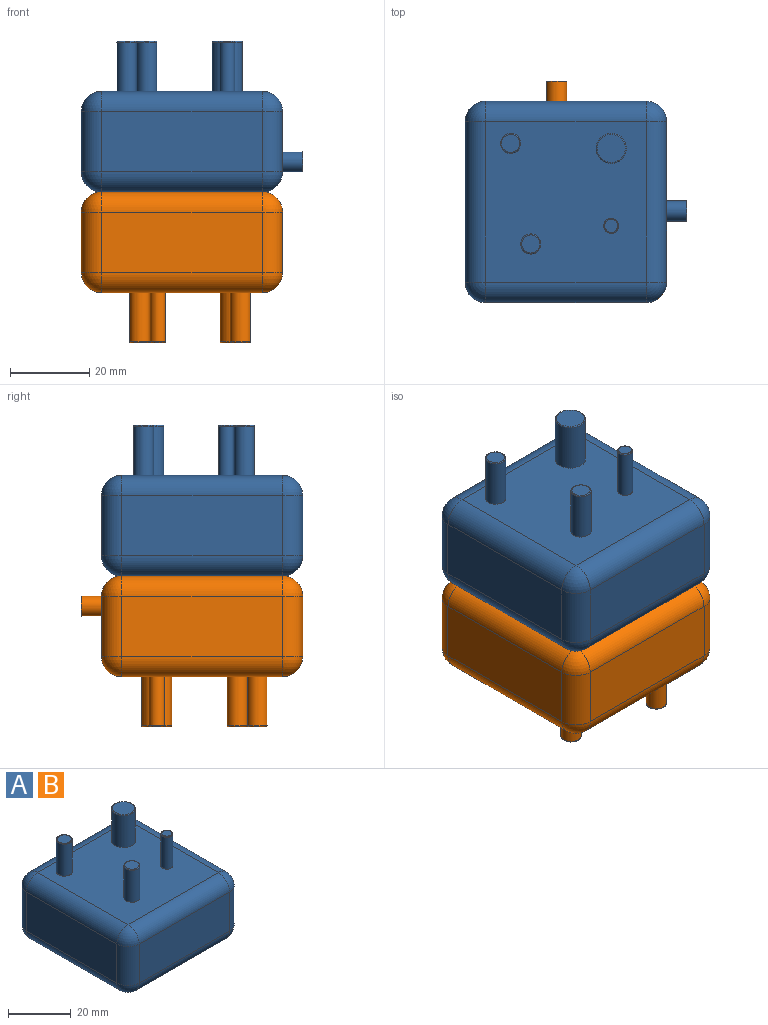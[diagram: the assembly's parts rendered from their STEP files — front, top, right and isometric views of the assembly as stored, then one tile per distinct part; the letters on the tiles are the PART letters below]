
ASSEMBLY  parts=2 mates=1
PART A: 40 faces, bbox 55.9x50.8x38.1 mm
  f0: plane 40.64x15.24mm, normal (0,1,0), area 619.4mm2, adj f26,f31,f34,f37
  f1: plane 40.64x15.24mm, normal (-1,0,0), area 619.4mm2, adj f23,f32,f33,f37
  f2: plane 40.64x15.24mm, normal (0,-1,0), area 619.4mm2, adj f18,f22,f23,f24
  f3: plane 40.64x15.24mm, normal (1,0,0), area 599.1mm2, adj f18,f21,f25,f26,f38
  f4: plane 40.64x40.64mm, normal (0,0,1), area 1554.1mm2, adj f6,f8,f10,f12,f21,f22,f31,f32
  f5: plane 40.64x40.64mm, normal (0,0,-1), area 1651.6mm2, adj f24,f25,f33,f34
  f6: cylinder r=2.54mm len=12.45mm, axis (0,0,-1), area 198.6mm2, adj f4,f17
  f7: plane 4.57x4.57mm, normal (0,0,1), area 16.4mm2, adj f17
  f8: cylinder r=3.81mm len=12.45mm, axis (0,0,-1), area 297.9mm2, adj f4,f16
  f9: plane 7.11x7.11mm, normal (0,0,1), area 39.7mm2, adj f16
  f10: cylinder r=2.54mm len=12.45mm, axis (0,0,-1), area 198.6mm2, adj f4,f14
  f11: plane 4.57x4.57mm, normal (0,0,1), area 16.4mm2, adj f14
  f12: cylinder r=1.91mm len=12.45mm, axis (0,0,-1), area 149mm2, adj f4,f15
  f13: plane 3.3x3.3mm, normal (0,0,1), area 8.6mm2, adj f15
  f14: torus R=2.29mm, axis (0,0,1), area 6.1mm2, adj f10,f11
  f15: torus R=1.65mm, axis (0,0,1), area 4.5mm2, adj f12,f13
  f16: torus R=3.56mm, axis (0,0,1), area 9.3mm2, adj f8,f9
  f17: torus R=2.29mm, axis (0,0,1), area 6.1mm2, adj f6,f7
  f18: cylinder r=5.08mm len=15.24mm, axis (0,0,1), area 121.6mm2, adj f2,f3,f19,f20
  f19: sphere r=5.08mm, area 40.5mm2, adj f18,f21,f22
  f20: sphere r=5.08mm, area 40.5mm2, adj f18,f24,f25
  f21: cylinder r=5.08mm len=40.64mm, axis (0,-1,0), area 324.3mm2, adj f3,f4,f19,f27
  f22: cylinder r=5.08mm len=40.64mm, axis (-1,0,0), area 324.3mm2, adj f2,f4,f19,f28
  f23: cylinder r=5.08mm len=15.24mm, axis (0,0,-1), area 121.6mm2, adj f1,f2,f28,f29
  f24: cylinder r=5.08mm len=40.64mm, axis (1,0,0), area 324.3mm2, adj f2,f5,f20,f29
  f25: cylinder r=5.08mm len=40.64mm, axis (0,1,0), area 324.3mm2, adj f3,f5,f20,f30
  f26: cylinder r=5.08mm len=15.24mm, axis (0,0,-1), area 121.6mm2, adj f0,f3,f27,f30
  f27: sphere r=5.08mm, area 40.5mm2, adj f21,f26,f31
  f28: sphere r=5.08mm, area 40.5mm2, adj f22,f23,f32
  f29: sphere r=5.08mm, area 40.5mm2, adj f23,f24,f33
  f30: sphere r=5.08mm, area 40.5mm2, adj f25,f26,f34
  f31: cylinder r=5.08mm len=40.64mm, axis (1,0,0), area 324.3mm2, adj f0,f4,f27,f35
  f32: cylinder r=5.08mm len=40.64mm, axis (0,1,0), area 324.3mm2, adj f1,f4,f28,f35
  f33: cylinder r=5.08mm len=40.64mm, axis (0,-1,0), area 324.3mm2, adj f1,f5,f29,f36
  f34: cylinder r=5.08mm len=40.64mm, axis (-1,0,0), area 324.3mm2, adj f0,f5,f30,f36
  f35: sphere r=5.08mm, area 40.5mm2, adj f31,f32,f37
  f36: sphere r=5.08mm, area 40.5mm2, adj f33,f34,f37
  f37: cylinder r=5.08mm len=15.24mm, axis (0,0,1), area 121.6mm2, adj f0,f1,f35,f36
  f38: cylinder r=2.54mm len=5.08mm, axis (-1,0,0), area 81.1mm2, adj f3,f39
  f39: plane 5.08x5.08mm, normal (1,0,0), area 20.3mm2, adj f38
PART B: same geometry as A
PLACE A t=(170.26,20.05,4.25)mm
PLACE B rot(axis=(0.71,0.71,0),180deg) t=(170.82,19.48,4.25)mm
MATE fastened B.f5 <-> A.f5  axis (0,0,1) through (173.12,22.35,4.25)mm
